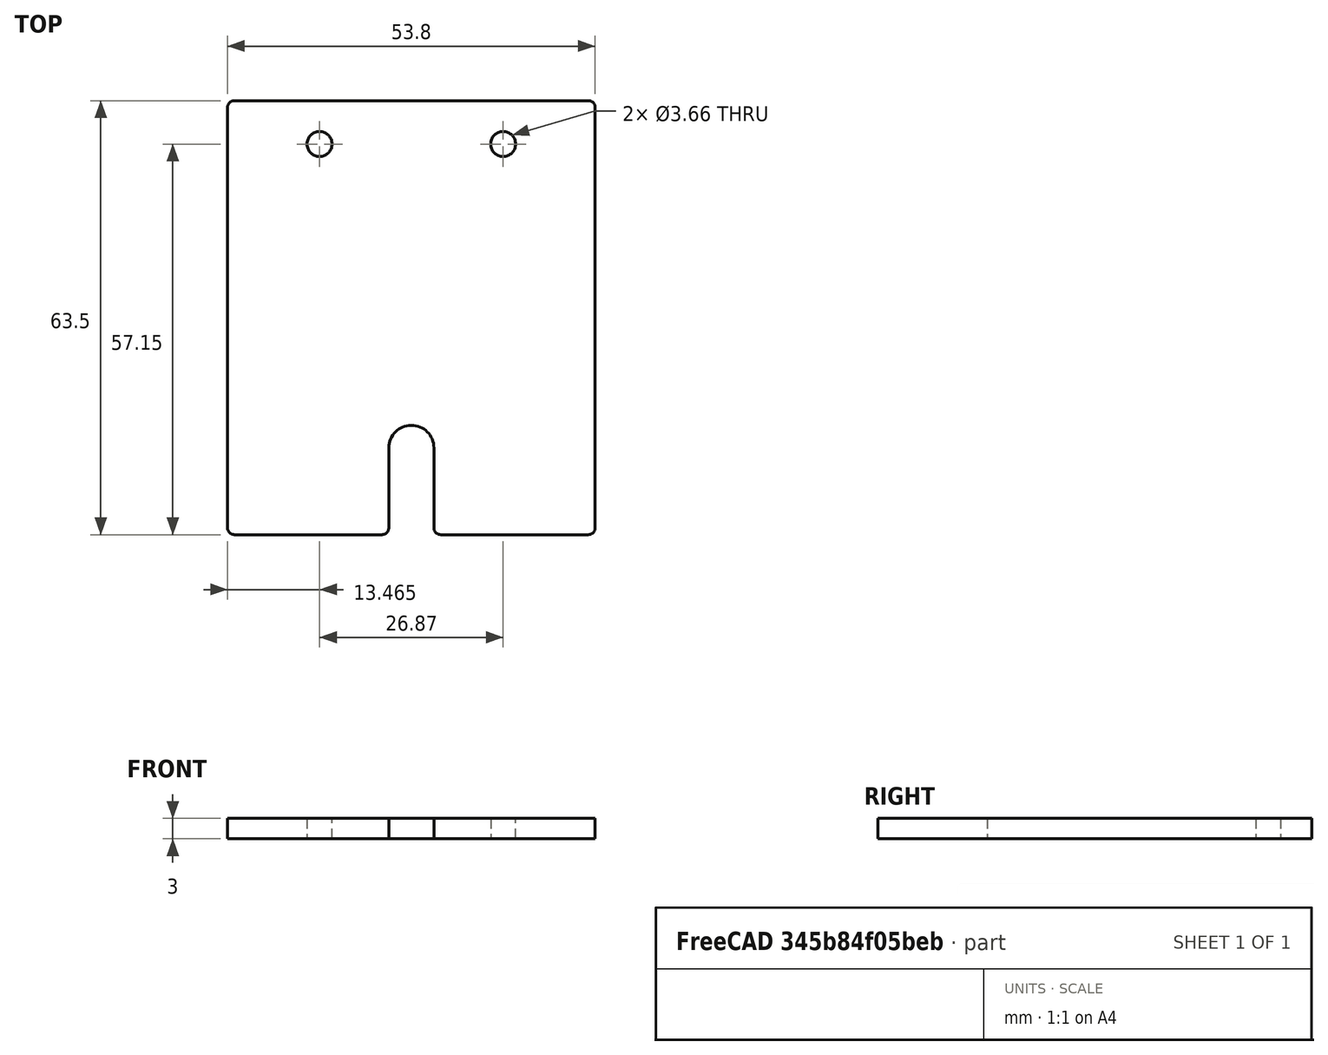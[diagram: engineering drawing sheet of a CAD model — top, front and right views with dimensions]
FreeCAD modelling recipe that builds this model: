
FCSTD DOCUMENT  (FreeCAD 0.21R33675 (Git))
Label: feeding_box_front_2p5in
License: All rights reserved
LicenseURL: http://en.wikipedia.org/wiki/All_rights_reserved
objects: Sketcher::SketchObject×1, Spreadsheet::Sheet×1, PartDesign::Pad×1, PartDesign::Body×1
note: 4 computed .brp shape members not serialized (recipe doc carries the construction recipe); baked Part::Feature solids carry a one-line shape summary decoded from their .brp

FEATURE [Sketcher::SketchObject] Sketch
  FullyConstrained = true
  MapMode = 5
  Support = -> [XY_Plane]
  expr: Constraints[19] = Spreadsheet.FilletRadius
  expr: Constraints[21] = Spreadsheet.Height
  expr: Constraints[22] = Spreadsheet.Length
  expr: Constraints[26] = Spreadsheet.MountHoleDistanceFromBottom
  expr: Constraints[27] = Spreadsheet.MountHoleDiameter
  expr: Constraints[31] = Spreadsheet.BracketHoleFromSide
  expr: Constraints[32] = Spreadsheet.UpperBracketHoleFromTop
  expr: Constraints[41] = Spreadsheet.BracketHoleDiameter
  expr: Constraints[68] = Spreadsheet.BracketHoleFromSide
  expr: Constraints[72] = Spreadsheet.UpperBracketHoleFromTop
  expr: Constraints[74] = Spreadsheet.BracketHoleDiameter
  sketch-geometry (30):
    g0: ArcOfCircle CenterX=-25.9 CenterY=30.75 CenterZ=0 NormalX=0 NormalY=0 NormalZ=1 AngleXU=0 Radius=1 StartAngle=1.5708 EndAngle=3.14159
    g1: LineSegment StartX=-25.9 StartY=31.75 StartZ=0 EndX=25.9 EndY=31.75 EndZ=0
    g2: ArcOfCircle CenterX=25.9 CenterY=30.75 CenterZ=0 NormalX=0 NormalY=0 NormalZ=1 AngleXU=0 Radius=1 StartAngle=-1.8e-15 EndAngle=1.5708
    g3: LineSegment StartX=26.9 StartY=30.75 StartZ=0 EndX=26.9 EndY=-30.75 EndZ=0
    g4: ArcOfCircle CenterX=25.9 CenterY=-30.75 CenterZ=0 NormalX=0 NormalY=0 NormalZ=1 AngleXU=0 Radius=1 StartAngle=4.71239 EndAngle=6.28319
    g5: LineSegment StartX=25.9 StartY=-31.75 StartZ=0 EndX=-25.9 EndY=-31.75 EndZ=0
    g6: ArcOfCircle CenterX=-25.9 CenterY=-30.75 CenterZ=0 NormalX=0 NormalY=0 NormalZ=1 AngleXU=0 Radius=1 StartAngle=3.14159 EndAngle=4.71239
    g7: LineSegment StartX=-26.9 StartY=-30.75 StartZ=0 EndX=-26.9 EndY=30.75 EndZ=0
    g8: GeomPoint X=-26.9 Y=31.75 Z=0
    g9: GeomPoint X=26.9 Y=-31.75 Z=0
    g10: Circle CenterX=0 CenterY=-19.05 CenterZ=0 NormalX=0 NormalY=0 NormalZ=1 AngleXU=0 Radius=3.302
    g11: LineSegment StartX=0 StartY=-19.05 StartZ=0 EndX=0 EndY=-31.75 EndZ=0
    g12: LineSegment StartX=-13.4352 StartY=31.75 StartZ=0 EndX=-13.4352 EndY=25.4 EndZ=0
    g13: LineSegment StartX=-13.4352 StartY=25.4 StartZ=0 EndX=-13.4352 EndY=0 EndZ=0
    g14: LineSegment StartX=-13.4352 StartY=-1.2e-15 StartZ=0 EndX=-26.9 EndY=-1.2e-15 EndZ=0
    g15: Circle CenterX=-13.4352 CenterY=25.4 CenterZ=0 NormalX=0 NormalY=0 NormalZ=1 AngleXU=0 Radius=1.8288
    g16: Circle CenterX=-13.4352 CenterY=-1.2e-15 CenterZ=0 NormalX=0 NormalY=0 NormalZ=1 AngleXU=0 Radius=1.8288
    g17: ArcOfCircle CenterX=0 CenterY=-19.05 CenterZ=0 NormalX=0 NormalY=0 NormalZ=1 AngleXU=0 Radius=3.302 StartAngle=0 EndAngle=3.14159
    g18: LineSegment StartX=-3.302 StartY=-19.05 StartZ=0 EndX=3.302 EndY=-19.05 EndZ=0
    g19: LineSegment StartX=-3.302 StartY=-19.05 StartZ=0 EndX=-3.302 EndY=-30.75 EndZ=0
    g20: LineSegment StartX=3.302 StartY=-19.05 StartZ=0 EndX=3.302 EndY=-30.75 EndZ=0
    g21: ArcOfCircle CenterX=-4.302 CenterY=-30.75 CenterZ=0 NormalX=0 NormalY=0 NormalZ=1 AngleXU=0 Radius=1 StartAngle=4.71239 EndAngle=6.28319
    g22: ArcOfCircle CenterX=4.302 CenterY=-30.75 CenterZ=0 NormalX=0 NormalY=0 NormalZ=1 AngleXU=0 Radius=1 StartAngle=3.14159 EndAngle=4.71239
    g23: LineSegment StartX=-25.9 StartY=-31.75 StartZ=0 EndX=-4.302 EndY=-31.75 EndZ=0
    g24: LineSegment StartX=4.302 StartY=-31.75 StartZ=0 EndX=25.9 EndY=-31.75 EndZ=0
    g25: LineSegment StartX=25.9 StartY=31.75 StartZ=0 EndX=26.9 EndY=31.75 EndZ=0
    g26: LineSegment StartX=26.9 StartY=30.75 StartZ=0 EndX=26.9 EndY=31.75 EndZ=0
    g27: LineSegment StartX=26.9 StartY=31.75 StartZ=0 EndX=13.4352 EndY=31.75 EndZ=0
    g28: LineSegment StartX=13.4352 StartY=31.75 StartZ=0 EndX=13.4352 EndY=25.4 EndZ=0
    g29: Circle CenterX=13.4352 CenterY=25.4 CenterZ=0 NormalX=0 NormalY=0 NormalZ=1 AngleXU=0 Radius=1.8288
  constraints (75):
    c: Tangent(g0,g1) = 1.5708
    c: Tangent(g1,g2) = 1.5708
    c: Tangent(g2,g3) = 1.5708
    c: Tangent(g3,g4) = 1.5708
    c: Tangent(g4,g5) = 1.5708
    c: Tangent(g5,g6) = 1.5708
    c: Tangent(g6,g7) = 1.5708
    c: Tangent(g7,g0) = 1.5708
    c: Horizontal(g1)
    c: Horizontal(g5)
    c: Vertical(g3)
    c: Vertical(g7)
    c: Equal(g0,g2)
    c: Equal(g2,g4)
    c: Equal(g4,g6)
    c: PointOnObject(g8,g1)
    c: PointOnObject(g8,g7)
    c: PointOnObject(g9,g3)
    c: PointOnObject(g9,g5)
    c: Radius(g2) = 1
    c: Symmetric(g8,g9,g-1)
    c: DistanceY(g4,g1) = 63.5
    c: DistanceX(g0,g2) = 53.8
    c: PointOnObject(g11,g5)
    c: PointOnObject(g11,g-2)
    c: Vertical(g11)
    c: DistanceY(g11,g11) = 12.7
    c: Diameter(g10) = 6.604
    c: Coincident(g10,g11)
    c: PointOnObject(g12,g1)
    c: Vertical(g12)
    c: DistanceX(g8,g12) = 13.4648
    c: DistanceY(g12,g12) = 6.35
    c: Coincident(g13,g12)
    c: Vertical(g13)
    c: Coincident(g14,g13)
    c: Horizontal(g14)
    c: Symmetric(g0,g6,g14)
    c: Coincident(g15,g12)
    c: Coincident(g16,g13)
    c: Equal(g15,g16)
    c: Diameter(g15) = 3.6576
    c: Coincident(g17,g10)
    c: Coincident(g18,g17)
    c: Coincident(g18,g17)
    c: Horizontal(g18)
    c: PointOnObject(g17,g18)
    c: PointOnObject(g17,g10)
    c: Coincident(g19,g17)
    c: Vertical(g19)
    c: Coincident(g20,g17)
    c: Vertical(g20)
    c: Equal(g19,g20)
    c: Tangent(g21,g19) = 1.5708
    c: Tangent(g21,g5) = 1.5708
    c: Tangent(g22,g20) = -1.5708
    c: Tangent(g22,g5) = 1.5708
    c: Equal(g22,g4)
    c: Coincident(g23,g6)
    c: Coincident(g23,g21)
    c: Coincident(g24,g22)
    c: Coincident(g24,g4)
    c: Coincident(g25,g1)
    c: Horizontal(g25)
    c: Coincident(g26,g2)
    c: Vertical(g26)
    c: Coincident(g26,g25)
    c: Coincident(g27,g25)
    c: DistanceX(g27,g27) = 13.4648
    c: Horizontal(g27)
    c: Vertical(g28)
    c: Coincident(g27,g28)
    c: DistanceY(g28,g28) = 6.35
    c: Coincident(g29,g28)
    c: Diameter(g29) = 3.6576
FEATURE [Spreadsheet::Sheet] Spreadsheet
  cells = A2='Parameters; A3='Height; B3(Height)==2.5 in; A4='Length; B4(Length)==53.8 mm; A5='Thickness; B5(Thickness)==3 mm; A6='FilletRadius; B6(FilletRadius)==1 mm; A7='MountHoleDiameter; B7(MountHoleDiameter)==0.26 in; A8='MountHoleDistanceFromBottom; B8(MountHoleDistanceFromBottom)==0.5 in; A10='BracketWidth; B10(BracketWidth)==0.5 in; A11='BracketHoleDiameter; B11(BracketHoleDiameter)==0.144 in; A12='BracketHoleOffset; B12(BracketHoleOffset)==0.412 in; A13='UpperBracketHoleFromTop; B13(UpperBracketHoleFromTop)==0.5 * BracketWidth; A14='BracketHoleFromSide; B14(BracketHoleFromSide)==BracketHoleOffset + Thickness
FEATURE [PartDesign::Pad] Pad
  Direction = (0,0,1)
  Length = 3
  Length2 = 10
  Profile = -> Sketch
  ReferenceAxis = -> Sketch [N_Axis]
  Type = 0
  expr: Length = Spreadsheet.Thickness
FEATURE [PartDesign::Body] Body
  Group = -> [Sketch,Pad]
  Origin = -> Origin
  Tip = -> Pad
